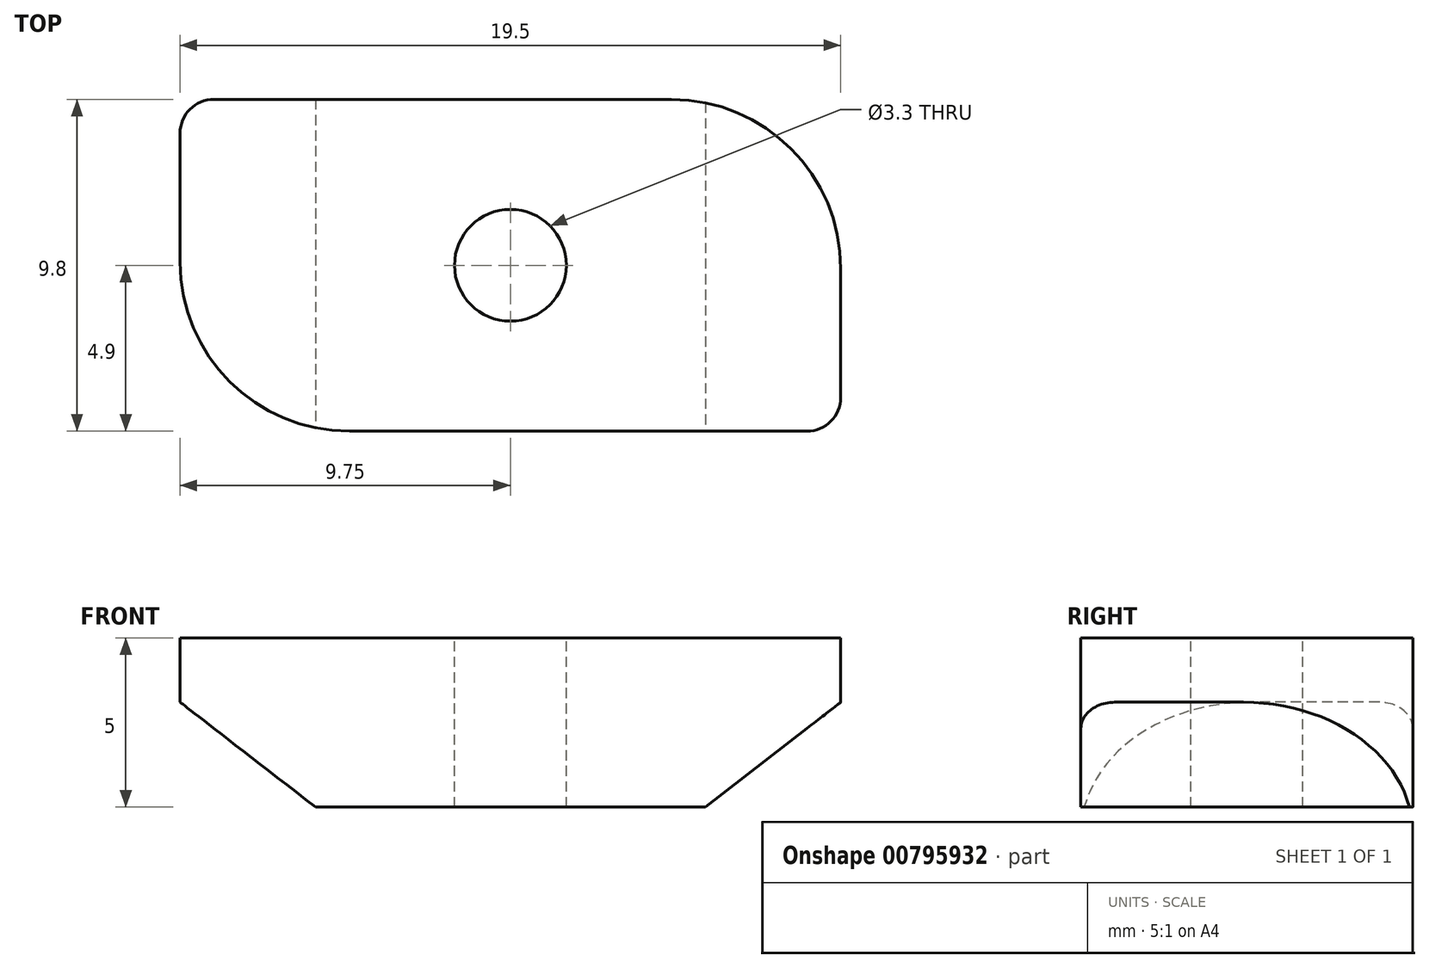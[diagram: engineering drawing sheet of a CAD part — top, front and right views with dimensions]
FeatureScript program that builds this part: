
annotation { "Feature Type Name" : "Feature", "Feature Type Description" : "" }
export const myFeature = defineFeature(function(context is Context, id is Id, definition is map)
    precondition{}
    {
        {
            var Q0;
            Q0=qCreatedBy(makeId("Top.planeOp"),FACE);
            var sketch = newSketch(context, id + "F0", { "sketchPlane" : qUnion([Q0])});
            skLineSegment(sketch, "E0.bottom", {"start": v(9.75, 4.9) * mm, "end": v(-9.75, 4.9) * mm});
            skLineSegment(sketch, "E0.top", {"start": v(9.75, -4.9) * mm, "end": v(-9.75, -4.9) * mm});
            skLineSegment(sketch, "E0.left", {"start": v(9.75, 4.9) * mm, "end": v(9.75, -4.9) * mm});
            skLineSegment(sketch, "E0.right", {"start": v(-9.75, 4.9) * mm, "end": v(-9.75, -4.9) * mm});
            skPoint(sketch, "E0.middle", {"position": v(0, 0) * mm});
            skSolve(sketch);
        }
        {
            var Q0;
            Q0 = qSketchRegion(id + "F0", true);
            extrude(context, id + "F1", {"entities" : qUnion([Q0]), "depth" : 5 * mm, "offsetDistance" : 25 * mm});
        }
        {
            var Q0;
            Q0=makeQuery(id+"F1.opExtrude","CAP_FACE",FACE,{"disambiguationData":[OSD([sQuery(id+"F0.wireOp",EDGE,"E0.bottom"),sQuery(id+"F0.wireOp",EDGE,"E0.top"),sQuery(id+"F0.wireOp",EDGE,"E0.left"),sQuery(id+"F0.wireOp",EDGE,"E0.right")])],"isStart":false});
            var sketch = newSketch(context, id + "F2", { "sketchPlane" : qUnion([Q0])});
            skPoint(sketch, "E1", {"position": v(0, 0) * mm});
            skSolve(sketch);
        }
        {
            var Q0;
            Q0=sQuery(id+"F2.wireOp",VERTEX,"E1");
            var Q1;
            Q1=makeQuery(id+"F1.opExtrude","SWEPT_BODY",BODY,{"disambiguationData":[OSD([sQuery(id+"F0.wireOp",EDGE,"E0.bottom"),sQuery(id+"F0.wireOp",EDGE,"E0.top"),sQuery(id+"F0.wireOp",EDGE,"E0.left"),sQuery(id+"F0.wireOp",EDGE,"E0.right")])]});
            hole(context, id + "F3", {"style" : HoleStyle.SIMPLE, "endStyle" : HoleEndStyle.THROUGH, "standardTappedOrClearance" : lookupTablePath({ "standard" : "ISO", "engagement" : "75%", "pitch" : "0.7 mm", "size" : "M4", "type" : "Tapped" }), "standardBlindInLast" : lookupTablePath({ "standard" : "ISO", "fit" : "Normal", "engagement" : "75%", "pitch" : "0.7 mm", "size" : "M4", "type" : "Clearance & tapped" }), "holeDiameter" : 3.3 * mm, "majorDiameter" : 4 * mm, "showTappedDepth" : true, "isTappedThrough" : true, "tappedDepth" : 12 * mm, "tapClearance" : 3, "locations" : qUnion([Q0]), "scope" : qUnion([Q1])});
        }
        {
            var Q0;
            Q0=makeQuery(id+"F1.opExtrude","SWEPT_EDGE",EDGE,{"disambiguationData":[OSD([sQuery(id+"F0.wireOp",EDGE,"E0.top"),sQuery(id+"F0.wireOp",EDGE,"E0.right")])]});
            var Q1;
            Q1=makeQuery(id+"F1.opExtrude","SWEPT_EDGE",EDGE,{"disambiguationData":[OSD([sQuery(id+"F0.wireOp",EDGE,"E0.bottom"),sQuery(id+"F0.wireOp",EDGE,"E0.left")])]});
            fillet(context, id + "F4", {"entities" : qUnion([Q0, Q1]), "radius" : 5 * mm, "tangentPropagation" : true, "allowEdgeOverflow" : false});
        }
        {
            var Q0;
            Q0=makeQuery(id+"F1.opExtrude","SWEPT_EDGE",EDGE,{"disambiguationData":[OSD([sQuery(id+"F0.wireOp",EDGE,"E0.bottom"),sQuery(id+"F0.wireOp",EDGE,"E0.right")])]});
            var Q1;
            Q1=makeQuery(id+"F1.opExtrude","SWEPT_EDGE",EDGE,{"disambiguationData":[OSD([sQuery(id+"F0.wireOp",EDGE,"E0.top"),sQuery(id+"F0.wireOp",EDGE,"E0.left")])]});
            fillet(context, id + "F5", {"entities" : qUnion([Q0, Q1]), "radius" : 1 * mm, "tangentPropagation" : true, "allowEdgeOverflow" : false});
        }
        {
            var Q0;
            Q0=qCreatedBy(makeId("Front.planeOp"),FACE);
            var sketch = newSketch(context, id + "F6", { "sketchPlane" : qUnion([Q0])});
            skLineSegment(sketch, "E2", {"start": v(5.75, 0) * mm, "end": v(9.75, 3.1) * mm});
            skLineSegment(sketch, "E3", {"start": v(9.75, 3.1) * mm, "end": v(9.75, 0) * mm});
            skLineSegment(sketch, "E4", {"start": v(9.75, 0) * mm, "end": v(5.75, 0) * mm});
            skLineSegment(sketch, "E5.MirrorCS", {"start": v(-9.75, 0) * mm, "end": v(-5.75, 0) * mm});
            skLineSegment(sketch, "E6.MirrorCS", {"start": v(-5.75, 0) * mm, "end": v(-9.75, 3.1) * mm});
            skLineSegment(sketch, "E7.MirrorCS", {"start": v(-9.75, 3.1) * mm, "end": v(-9.75, 0) * mm});
            skSolve(sketch);
        }
        {
            var Q0;
            Q0 = qSketchRegion(id + "F6", true);
            extrude(context, id + "F7", {"entities" : qUnion([Q0]), "operationType" : NewBodyOperationType.REMOVE, "endBound" : BoundingType.THROUGH_ALL, "oppositeDirection" : true, "depth" : 25 * mm, "offsetDistance" : 25 * mm, "hasSecondDirection" : true, "secondDirectionBound" : SecondDirectionBoundingType.THROUGH_ALL, "secondDirectionOppositeDirection" : false, "secondDirectionDepth" : 25 * mm});
        }
    });
